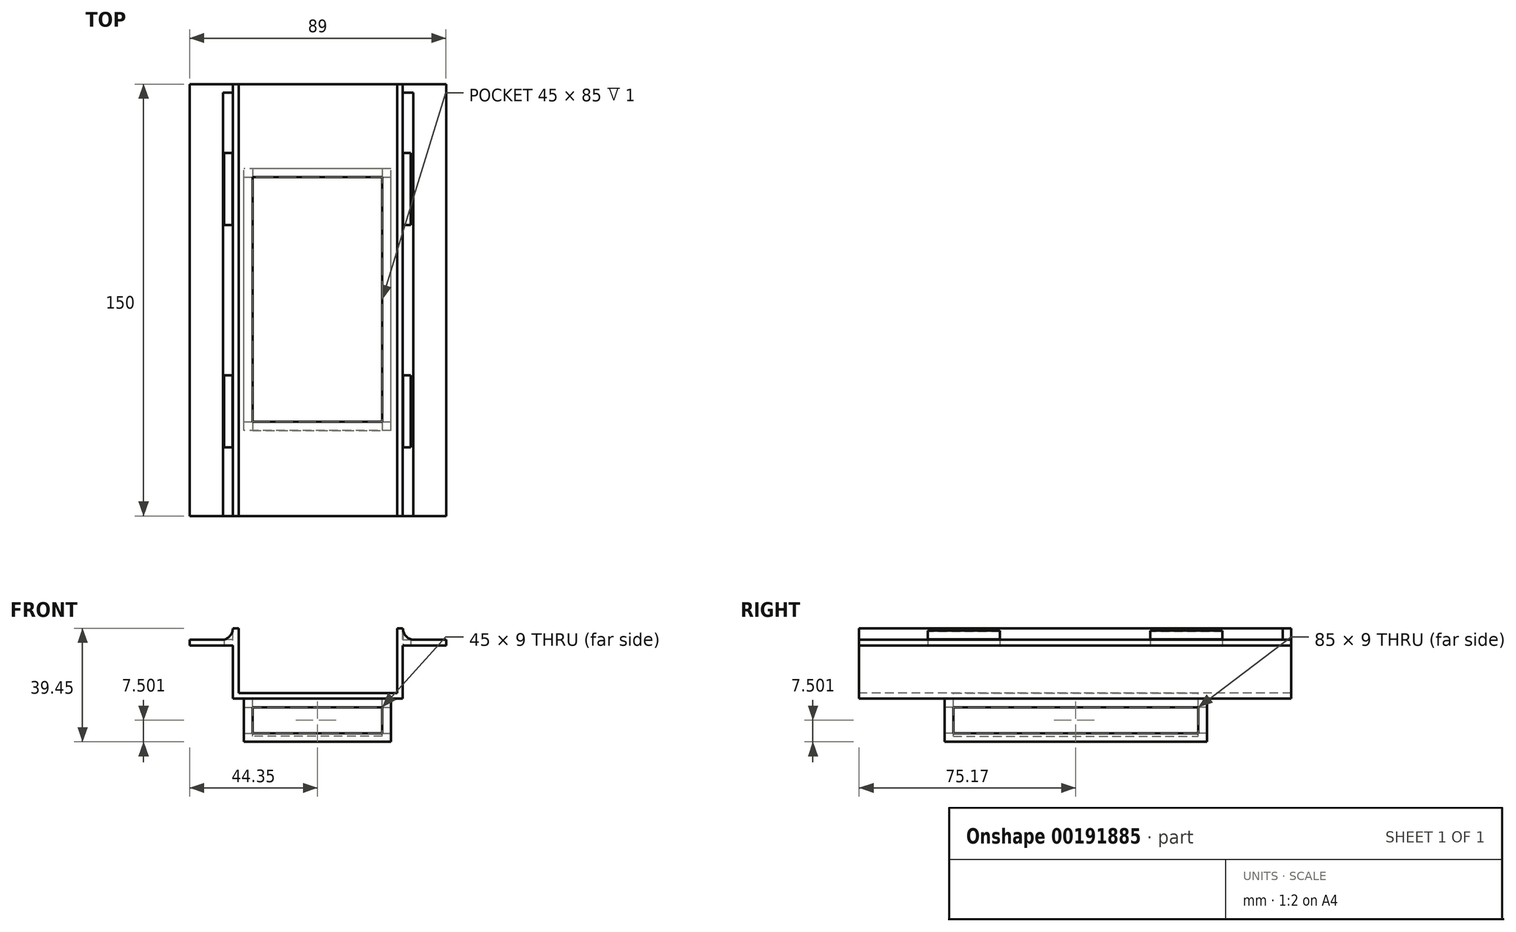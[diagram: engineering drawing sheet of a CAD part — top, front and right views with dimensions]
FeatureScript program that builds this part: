
annotation { "Feature Type Name" : "Feature", "Feature Type Description" : "" }
export const myFeature = defineFeature(function(context is Context, id is Id, definition is map)
    precondition{}
    {
        {
            var Q0;
            Q0=qCreatedBy(makeId("Front.planeOp"),FACE);
            var sketch = newSketch(context, id + "F0", { "sketchPlane" : qUnion([Q0])});
            skLineSegment(sketch, "E0.bottom", {"start": v(29.65, -10.12) * mm, "end": v(-29.35, -10.12) * mm});
            skLineSegment(sketch, "E0.left", {"start": v(29.65, -10.12) * mm, "end": v(29.65, 10.33) * mm});
            skLineSegment(sketch, "E0.right", {"start": v(-29.35, -10.12) * mm, "end": v(-29.35, 10.33) * mm});
            skPoint(sketch, "E0.middle", {"position": v(0.15, 0.1) * mm});
            skLineSegment(sketch, "E1.left", {"start": v(27.65, -9) * mm, "end": v(27.65, 9.22) * mm});
            skLineSegment(sketch, "E1.right", {"start": v(-27.35, -9) * mm, "end": v(-27.35, 9.22) * mm});
            skLineSegment(sketch, "E2", {"start": v(-27.35, 9.22) * mm, "end": v(-27.35, 10.33) * mm});
            skLineSegment(sketch, "E3", {"start": v(27.65, 9.22) * mm, "end": v(27.65, 10.33) * mm});
            skLineSegment(sketch, "E4.left", {"start": v(-24.65, 1.23) * mm, "end": v(-24.65, 1.23) * mm});
            skLineSegment(sketch, "E4.right", {"start": v(-22.65, 1.23) * mm, "end": v(-22.65, 1.23) * mm});
            skLineSegment(sketch, "E5", {"start": v(-29.35, 10.33) * mm, "end": v(-29.35, 14.33) * mm});
            skLineSegment(sketch, "E6", {"start": v(-29.35, 14.33) * mm, "end": v(-27.35, 14.33) * mm});
            skLineSegment(sketch, "E7", {"start": v(-27.35, 14.33) * mm, "end": v(-27.35, -9) * mm});
            skLineSegment(sketch, "E8", {"start": v(29.65, 10.33) * mm, "end": v(29.65, 14.33) * mm});
            skLineSegment(sketch, "E9", {"start": v(29.65, 14.33) * mm, "end": v(27.65, 14.33) * mm});
            skLineSegment(sketch, "E10", {"start": v(27.65, 14.33) * mm, "end": v(27.65, -9) * mm});
            skLineSegment(sketch, "E11", {"start": v(-27.35, -8.12) * mm, "end": v(27.65, -8.12) * mm});
            skLineSegment(sketch, "E12.bottom", {"start": v(-29.35, 10.33) * mm, "end": v(-44.35, 10.33) * mm});
            skLineSegment(sketch, "E12.top", {"start": v(-29.35, 8.33) * mm, "end": v(-44.35, 8.33) * mm});
            skLineSegment(sketch, "E12.left", {"start": v(-29.35, 10.33) * mm, "end": v(-29.35, 8.33) * mm});
            skLineSegment(sketch, "E12.right", {"start": v(-44.35, 10.33) * mm, "end": v(-44.35, 8.33) * mm});
            skLineSegment(sketch, "E13.bottom", {"start": v(29.65, 10.33) * mm, "end": v(44.65, 10.33) * mm});
            skLineSegment(sketch, "E13.top", {"start": v(29.65, 8.33) * mm, "end": v(44.65, 8.33) * mm});
            skLineSegment(sketch, "E13.left", {"start": v(29.65, 10.33) * mm, "end": v(29.65, 8.33) * mm});
            skLineSegment(sketch, "E13.right", {"start": v(44.65, 10.33) * mm, "end": v(44.65, 8.33) * mm});
            skLineSegment(sketch, "E14.right", {"start": v(-30.69, 10.34) * mm, "end": v(-30.69, 8.34) * mm});
            skLineSegment(sketch, "E15.right", {"start": v(41.5, 10.34) * mm, "end": v(41.5, 8.34) * mm});
            skLineSegment(sketch, "E16", {"start": v(0, 35.06) * mm, "end": v(0, -19.3) * mm, "construction": true});
            skArc(sketch, "E17", {"start": v(29.65, 14.33) * mm, "mid": v(30.7, 11.61) * mm, "end": v(33.32, 10.33) * mm});
            skArc(sketch, "E18", {"start": v(-32.7, 10.33) * mm, "mid": v(-30.3, 11.72) * mm, "end": v(-29.35, 14.33) * mm});
            skSolve(sketch);
        }
        {
            var Q0;
            Q0=makeQuery(id+"F0.imprint","IMPRINT",FACE,{"disambiguationData":[TD([[makeQuery(id+"F0.imprint","IMPRINT",EDGE,{"derivedFrom":sQuery(id+"F0.wireOp",EDGE,"E12.top")}),-1.0]])]});
            var Q1;
            Q1=makeQuery(id+"F0.imprint","IMPRINT",FACE,{"disambiguationData":[TD([[makeQuery(id+"F0.imprint","IMPRINT",EDGE,{"derivedFrom":sQuery(id+"F0.wireOp",EDGE,"E0.bottom")}),-1.0]])]});
            var Q2;
            Q2=makeQuery(id+"F0.imprint","IMPRINT",FACE,{"disambiguationData":[TD([[makeQuery(id+"F0.imprint","IMPRINT",EDGE,{"derivedFrom":sQuery(id+"F0.wireOp",EDGE,"E13.top")}),1.0]])]});
            extrude(context, id + "F1", {"entities" : qUnion([Q0, Q1, Q2]), "oppositeDirection" : true, "depth" : 150 * mm});
        }
        {
            var Q0;
            {var subQ0=sQuery(id+"F0.wireOp",EDGE,"E8");Q0=makeQuery(id+"F0.imprint","IMPRINT",FACE,{"disambiguationData":[TD([[makeQuery(id+"F0.imprint","IMPRINT",EDGE,{"derivedFrom":subQ0}),-1.0]])]});}
            var Q1;
            {var subQ0=sQuery(id+"F0.wireOp",EDGE,"E5");Q1=makeQuery(id+"F0.imprint","IMPRINT",FACE,{"disambiguationData":[TD([[makeQuery(id+"F0.imprint","IMPRINT",EDGE,{"derivedFrom":subQ0}),1.0]])]});}
            extrude(context, id + "F2", {"entities" : qUnion([Q0, Q1]), "operationType" : NewBodyOperationType.ADD, "oppositeDirection" : true, "depth" : 147 * mm});
        }
        {
            var Q0;
            Q0=makeQuery(id+"F1.opExtrude","SWEPT_FACE",FACE,{"disambiguationData":[OSD([sQuery(id+"F0.wireOp",EDGE,"E11")])]});
            var sketch = newSketch(context, id + "F3", { "sketchPlane" : qUnion([Q0])});
            skLineSegment(sketch, "E19.bottom", {"start": v(22.5, 32.67) * mm, "end": v(-22.5, 32.67) * mm});
            skLineSegment(sketch, "E19.top", {"start": v(22.5, 117.67) * mm, "end": v(-22.5, 117.67) * mm});
            skLineSegment(sketch, "E19.left", {"start": v(22.5, 32.67) * mm, "end": v(22.5, 117.67) * mm});
            skLineSegment(sketch, "E19.right", {"start": v(-22.5, 32.67) * mm, "end": v(-22.5, 117.67) * mm});
            skPoint(sketch, "E19.middle", {"position": v(0, 75.17) * mm});
            skLineSegment(sketch, "E20.0", {"start": v(25.5, 120.67) * mm, "end": v(-25.5, 120.67) * mm});
            skLineSegment(sketch, "E20.1", {"start": v(25.5, 29.67) * mm, "end": v(25.5, 120.67) * mm});
            skLineSegment(sketch, "E20.2", {"start": v(25.5, 29.67) * mm, "end": v(-25.5, 29.67) * mm});
            skLineSegment(sketch, "E20.3", {"start": v(-25.5, 29.67) * mm, "end": v(-25.5, 120.67) * mm});
            skSolve(sketch);
        }
        {
            var Q0;
            Q0=makeQuery(id+"F3.imprint","IMPRINT",FACE,{"disambiguationData":[TD([[makeQuery(id+"F3.imprint","IMPRINT",EDGE,{"derivedFrom":sQuery(id+"F3.wireOp",EDGE,"E19.bottom")}),-1.0]])]});
            var Q1;
            Q1=makeQuery(id+"F3.imprint","IMPRINT",FACE,{"disambiguationData":[TD([[makeQuery(id+"F3.imprint","IMPRINT",EDGE,{"derivedFrom":sQuery(id+"F3.wireOp",EDGE,"E19.bottom")}),1.0]])]});
            extrude(context, id + "F4", {"entities" : qUnion([Q0, Q1]), "operationType" : NewBodyOperationType.ADD, "oppositeDirection" : true, "depth" : 17 * mm});
        }
        {
            var Q0;
            Q0=makeQuery(id+"F3.imprint","IMPRINT",FACE,{"disambiguationData":[TD([[makeQuery(id+"F3.imprint","IMPRINT",EDGE,{"derivedFrom":sQuery(id+"F3.wireOp",EDGE,"E19.bottom")}),-1.0]])]});
            extrude(context, id + "F5", {"entities" : qUnion([Q0]), "operationType" : NewBodyOperationType.REMOVE, "oppositeDirection" : true, "depth" : 15 * mm});
        }
        {
            var Q0;
            Q0=makeQuery(id+"F4.opExtrude","SWEPT_FACE",FACE,{"disambiguationData":[OSD([sQuery(id+"F3.wireOp",EDGE,"E20.1")])]});
            var sketch = newSketch(context, id + "F6", { "sketchPlane" : qUnion([Q0])});
            skLineSegment(sketch, "E21.0", {"start": v(117.67, -13.12) * mm, "end": v(32.67, -13.12) * mm});
            skLineSegment(sketch, "E21.1", {"start": v(117.67, -22.12) * mm, "end": v(117.67, -13.12) * mm});
            skLineSegment(sketch, "E21.2", {"start": v(32.67, -22.12) * mm, "end": v(117.67, -22.12) * mm});
            skLineSegment(sketch, "E21.3", {"start": v(32.67, -13.12) * mm, "end": v(32.67, -22.12) * mm});
            skSolve(sketch);
        }
        {
            var Q0;
            Q0=makeQuery(id+"F6.imprint","IMPRINT",FACE,{"disambiguationData":[TD([[makeQuery(id+"F6.imprint","IMPRINT",EDGE,{"derivedFrom":sQuery(id+"F6.wireOp",EDGE,"E21.0")}),1.0]])]});
            extrude(context, id + "F7", {"entities" : qUnion([Q0]), "operationType" : NewBodyOperationType.REMOVE, "oppositeDirection" : true, "depth" : 75 * mm});
        }
        {
            var Q0;
            Q0=makeQuery(id+"F4.opExtrude","SWEPT_FACE",FACE,{"disambiguationData":[OSD([sQuery(id+"F3.wireOp",EDGE,"E20.2")])]});
            var sketch = newSketch(context, id + "F8", { "sketchPlane" : qUnion([Q0])});
            skLineSegment(sketch, "E22.0", {"start": v(22.5, -22.12) * mm, "end": v(22.5, -13.12) * mm});
            skLineSegment(sketch, "E22.1", {"start": v(-22.5, -22.12) * mm, "end": v(22.5, -22.12) * mm});
            skLineSegment(sketch, "E22.2", {"start": v(-22.5, -13.12) * mm, "end": v(-22.5, -22.12) * mm});
            skLineSegment(sketch, "E22.3", {"start": v(22.5, -13.12) * mm, "end": v(-22.5, -13.12) * mm});
            skSolve(sketch);
        }
        {
            var Q0;
            Q0=makeQuery(id+"F8.imprint","IMPRINT",FACE,{"disambiguationData":[TD([[makeQuery(id+"F8.imprint","IMPRINT",EDGE,{"derivedFrom":sQuery(id+"F8.wireOp",EDGE,"E22.0")}),1.0]])]});
            extrude(context, id + "F9", {"entities" : qUnion([Q0]), "operationType" : NewBodyOperationType.REMOVE, "oppositeDirection" : true, "depth" : 95 * mm});
        }
        {
            var Q0;
            Q0=makeQuery(id+"F1.opExtrude","SWEPT_FACE",FACE,{"disambiguationData":[OSD([sQuery(id+"F0.wireOp",EDGE,"E12.top")])]});
            var sketch = newSketch(context, id + "F10", { "sketchPlane" : qUnion([Q0])});
            skLineSegment(sketch, "E23.bottom", {"start": v(-29.73, -23.9) * mm, "end": v(-32.35, -23.9) * mm});
            skLineSegment(sketch, "E23.top", {"start": v(-29.73, -48.9) * mm, "end": v(-32.35, -48.9) * mm});
            skLineSegment(sketch, "E23.right", {"start": v(-32.35, -23.9) * mm, "end": v(-32.35, -48.9) * mm});
            skLineSegment(sketch, "E24", {"start": v(0, 0) * mm, "end": v(0, -121.16) * mm, "construction": true});
            skLineSegment(sketch, "E25.MirrorCS", {"start": v(29.73, -23.9) * mm, "end": v(32.35, -23.9) * mm});
            skLineSegment(sketch, "E26.MirrorCS", {"start": v(29.73, -48.9) * mm, "end": v(32.35, -48.9) * mm});
            skLineSegment(sketch, "E27.MirrorCS", {"start": v(32.35, -23.9) * mm, "end": v(32.35, -48.9) * mm});
            skLineSegment(sketch, "E28", {"start": v(29.73, -23.9) * mm, "end": v(29.73, -48.9) * mm});
            skPoint(sketch, "E29.orphan", {"position": v(29.35, -23.9) * mm});
            skPoint(sketch, "E30.orphan", {"position": v(29.35, -48.9) * mm});
            skPoint(sketch, "E31.orphan", {"position": v(-29.35, -23.9) * mm});
            skPoint(sketch, "E32.orphan", {"position": v(-29.35, -48.9) * mm});
            skLineSegment(sketch, "E33", {"start": v(-29.52, -23.9) * mm, "end": v(-29.52, -48.87) * mm});
            skLineSegment(sketch, "E34", {"start": v(-29.52, -48.87) * mm, "end": v(-29.52, -48.9) * mm});
            skLineSegment(sketch, "E35", {"start": v(-29.52, -48.9) * mm, "end": v(-29.73, -48.9) * mm});
            skLineSegment(sketch, "E36", {"start": v(-29.73, -23.9) * mm, "end": v(-29.52, -23.9) * mm});
            skLineSegment(sketch, "E37", {"start": v(-44.35, -75) * mm, "end": v(44.59, -75) * mm, "construction": true});
            skLineSegment(sketch, "E38.MirrorCS", {"start": v(29.73, -101.1) * mm, "end": v(32.35, -101.1) * mm});
            skLineSegment(sketch, "E39.MirrorCS", {"start": v(29.73, -126.1) * mm, "end": v(32.35, -126.1) * mm});
            skPoint(sketch, "E40.MirrorP", {"position": v(29.35, -101.1) * mm});
            skLineSegment(sketch, "E41.MirrorCS", {"start": v(29.73, -126.1) * mm, "end": v(29.73, -101.1) * mm});
            skPoint(sketch, "E42.MirrorP", {"position": v(29.35, -126.1) * mm});
            skLineSegment(sketch, "E43.MirrorCS", {"start": v(32.35, -126.1) * mm, "end": v(32.35, -101.1) * mm});
            skLineSegment(sketch, "E44.MirrorCS", {"start": v(-29.52, -101.1) * mm, "end": v(-29.73, -101.1) * mm});
            skLineSegment(sketch, "E45.MirrorCS", {"start": v(-29.52, -101.13) * mm, "end": v(-29.52, -101.1) * mm});
            skLineSegment(sketch, "E46.MirrorCS", {"start": v(-29.73, -126.1) * mm, "end": v(-29.52, -126.1) * mm});
            skLineSegment(sketch, "E47.MirrorCS", {"start": v(-29.73, -126.1) * mm, "end": v(-32.35, -126.1) * mm});
            skLineSegment(sketch, "E48.MirrorCS", {"start": v(-29.73, -101.1) * mm, "end": v(-32.35, -101.1) * mm});
            skLineSegment(sketch, "E49.MirrorCS", {"start": v(-32.35, -126.1) * mm, "end": v(-32.35, -101.1) * mm});
            skLineSegment(sketch, "E50.MirrorCS", {"start": v(-29.52, -126.1) * mm, "end": v(-29.52, -101.13) * mm});
            skPoint(sketch, "E51.MirrorP", {"position": v(-29.35, -101.1) * mm});
            skPoint(sketch, "E52.MirrorP", {"position": v(-29.35, -126.1) * mm});
            skSolve(sketch);
        }
        {
            var Q0;
            Q0=qSketchRegion(id+"F10",true);
            extrude(context, id + "F11", {"entities" : qUnion([Q0]), "operationType" : NewBodyOperationType.REMOVE, "oppositeDirection" : true, "depth" : 25 * mm});
        }
    });
